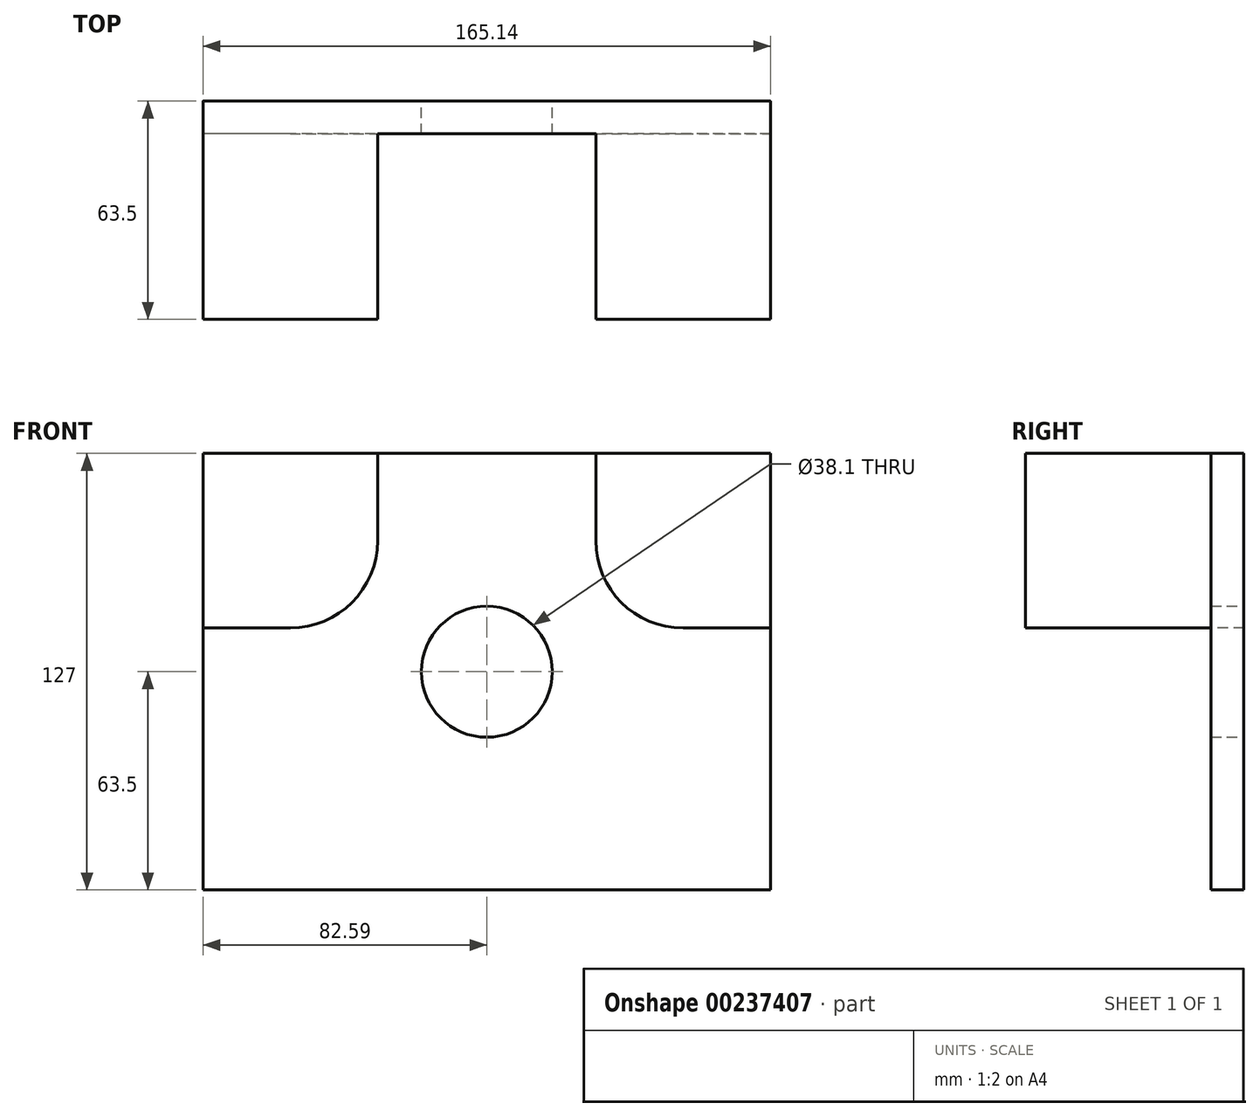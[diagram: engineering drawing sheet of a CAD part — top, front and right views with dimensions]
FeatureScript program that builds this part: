
annotation { "Feature Type Name" : "Feature", "Feature Type Description" : "" }
export const myFeature = defineFeature(function(context is Context, id is Id, definition is map)
    precondition{}
    {
        {
            var Q0;
            Q0=qCreatedBy(makeId("Front.planeOp"),FACE);
            var sketch = newSketch(context, id + "F0", { "sketchPlane" : qUnion([Q0])});
            skLineSegment(sketch, "E0.bottom", {"start": v(82.55, 63.5) * mm, "end": v(-82.55, 63.5) * mm});
            skLineSegment(sketch, "E0.top", {"start": v(82.55, -63.5) * mm, "end": v(-82.55, -63.5) * mm});
            skLineSegment(sketch, "E0.left", {"start": v(82.55, 63.5) * mm, "end": v(82.55, -63.5) * mm});
            skLineSegment(sketch, "E0.right", {"start": v(-82.55, 63.5) * mm, "end": v(-82.55, -63.5) * mm});
            skPoint(sketch, "E0.middle", {"position": v(0, 0) * mm});
            skSolve(sketch);
        }
        {
            var Q0;
            Q0 = qSketchRegion(id + "F0", true);
            extrude(context, id + "F1", {"entities" : qUnion([Q0]), "depth" : 9.52 * mm});
        }
        {
            var Q0;
            Q0=sQuery(id+"F0.wireOp",VERTEX,"E0.middle");
            var Q1;
            Q1=makeQuery(id+"F1.opExtrude","SWEPT_BODY",BODY,{"disambiguationData":[OSD([sQuery(id+"F0.wireOp",EDGE,"E0.bottom"),sQuery(id+"F0.wireOp",EDGE,"E0.top"),sQuery(id+"F0.wireOp",EDGE,"E0.left"),sQuery(id+"F0.wireOp",EDGE,"E0.right")])]});
            hole(context, id + "F2", {"style" : HoleStyle.SIMPLE, "endStyle" : HoleEndStyle.THROUGH, "oppositeDirection" : true, "holeDiameter" : 38.1 * mm, "locations" : qUnion([Q0]), "scope" : qUnion([Q1]), "isTappedThrough" : true});
        }
        {
            var Q0;
            Q0=qCreatedBy(makeId("Front.planeOp"),FACE);
            var sketch = newSketch(context, id + "F3", { "sketchPlane" : qUnion([Q0])});
            skLineSegment(sketch, "E1.bottom", {"start": v(-82.6, 63.5) * mm, "end": v(-31.8, 63.5) * mm});
            skLineSegment(sketch, "E1.top", {"start": v(-82.6, 12.7) * mm, "end": v(-31.8, 12.7) * mm});
            skLineSegment(sketch, "E1.left", {"start": v(-82.6, 63.5) * mm, "end": v(-82.6, 12.7) * mm});
            skLineSegment(sketch, "E1.right", {"start": v(-31.8, 63.5) * mm, "end": v(-31.8, 12.7) * mm});
            skLineSegment(sketch, "E2.bottom", {"start": v(82.5, 63.5) * mm, "end": v(31.7, 63.5) * mm});
            skLineSegment(sketch, "E2.top", {"start": v(82.5, 12.7) * mm, "end": v(31.7, 12.7) * mm});
            skLineSegment(sketch, "E2.left", {"start": v(82.5, 63.5) * mm, "end": v(82.5, 12.7) * mm});
            skLineSegment(sketch, "E2.right", {"start": v(31.7, 63.5) * mm, "end": v(31.7, 12.7) * mm});
            skSolve(sketch);
        }
        {
            var Q0;
            Q0 = qSketchRegion(id + "F3", true);
            extrude(context, id + "F4", {"entities" : qUnion([Q0]), "operationType" : NewBodyOperationType.ADD, "depth" : 63.5 * mm});
        }
        {
            var Q0;
            Q0=makeQuery(id+"F4.opExtrude","SWEPT_EDGE",EDGE,{"disambiguationData":[OSD([sQuery(id+"F3.wireOp",EDGE,"E1.top"),sQuery(id+"F3.wireOp",EDGE,"E1.right")])]});
            var Q1;
            Q1=makeQuery(id+"F4.opExtrude","SWEPT_EDGE",EDGE,{"disambiguationData":[OSD([sQuery(id+"F3.wireOp",EDGE,"E2.top"),sQuery(id+"F3.wireOp",EDGE,"E2.right")])]});
            fillet(context, id + "F5", {"entities" : qUnion([Q0, Q1]), "radius" : 25.4 * mm, "tangentPropagation" : true, "allowEdgeOverflow" : false});
        }
    });
